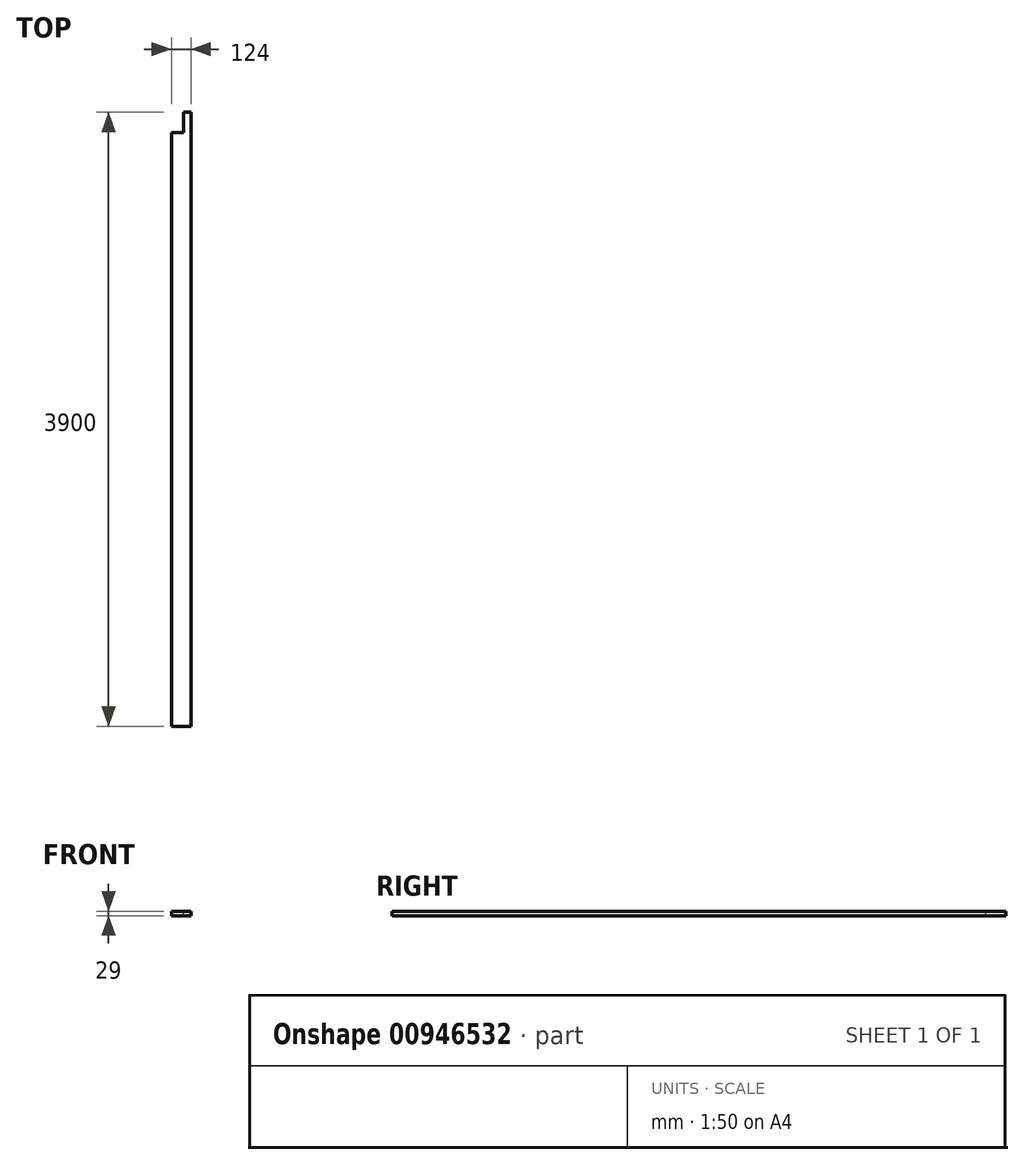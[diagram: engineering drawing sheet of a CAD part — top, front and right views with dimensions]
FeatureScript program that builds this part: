
annotation { "Feature Type Name" : "Feature", "Feature Type Description" : "" }
export const myFeature = defineFeature(function(context is Context, id is Id, definition is map)
    precondition{}
    {
        {
            var Q0;
            Q0=qCreatedBy(makeId("Front.planeOp"),FACE);
            var sketch = newSketch(context, id + "F0", { "sketchPlane" : qUnion([Q0])});
            skLineSegment(sketch, "E0.bottom", {"start": v(0, 0) * mm, "end": v(124, 0) * mm});
            skLineSegment(sketch, "E0.top", {"start": v(0, 29) * mm, "end": v(124, 29) * mm});
            skLineSegment(sketch, "E0.left", {"start": v(0, 0) * mm, "end": v(0, 29) * mm});
            skLineSegment(sketch, "E0.right", {"start": v(124, 0) * mm, "end": v(124, 29) * mm});
            skSolve(sketch);
        }
        {
            var Q0;
            Q0=qSketchRegion(id+"F0",true);
            extrude(context, id + "F1", {"entities" : qUnion([Q0]), "depth" : 3900 * mm, "offsetDistance" : 25 * mm});
        }
        {
            var Q0;
            Q0=makeQuery(id+"F1.opExtrude","SWEPT_FACE",FACE,{"disambiguationData":[OSD([sQuery(id+"F0.wireOp",EDGE,"E0.top")])]});
            var sketch = newSketch(context, id + "F2", { "sketchPlane" : qUnion([Q0])});
            skLineSegment(sketch, "E1.bottom", {"start": v(0, 0) * mm, "end": v(77, 0) * mm});
            skLineSegment(sketch, "E1.top", {"start": v(0, -128) * mm, "end": v(77, -128) * mm});
            skLineSegment(sketch, "E1.left", {"start": v(0, 0) * mm, "end": v(0, -128) * mm});
            skLineSegment(sketch, "E1.right", {"start": v(77, 0) * mm, "end": v(77, -128) * mm});
            skSolve(sketch);
        }
        {
            var Q0;
            Q0 = qSketchRegion(id + "F2", true);
            var Q1;
            Q1=makeQuery(id+"F1.opExtrude","SWEPT_FACE",FACE,{"disambiguationData":[OSD([sQuery(id+"F0.wireOp",EDGE,"E0.bottom")])]});
            extrude(context, id + "F3", {"entities" : qUnion([Q0]), "operationType" : NewBodyOperationType.REMOVE, "endBound" : BoundingType.UP_TO_SURFACE, "oppositeDirection" : true, "depth" : 25 * mm, "endBoundEntityFace" : qUnion([Q1]), "offsetDistance" : 25 * mm});
        }
    });
